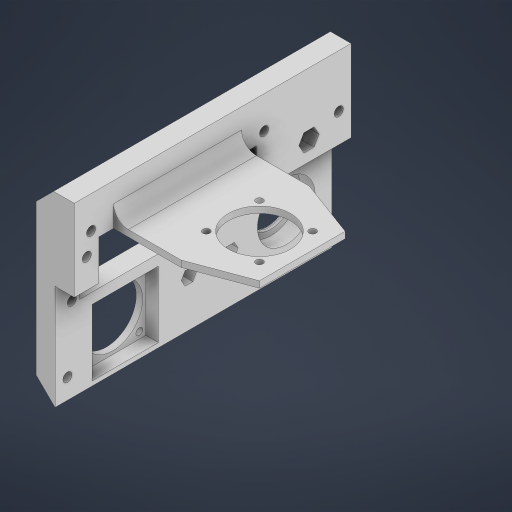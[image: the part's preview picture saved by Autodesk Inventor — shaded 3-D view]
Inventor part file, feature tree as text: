
AUTODESK INVENTOR PART (.ipt)
format: ipt  version: 2024 (Build 280153000, 153)  size: 458,240 bytes
history: native  units: in
note: dims shown in document units (in); Inventor stores cm internally (conversion verified against a paired STEP export)
features: reference x18, extrude x14, sketch x12, other x9, projected_geometry x7, fillet x2, plane x1, chamfer x1
ambient origin geometry x8: Origin, YZ Plane, XZ Plane, XY Plane, X Axis, Y Axis, Z Axis, Center Point
bodies: Solid1 (feature_tree)
feature tree (64):
  sketch  "Sketch1"  dims[d0=0.0787in d1=0.0079in]
  plane  "Work Plane1"
  extrude  "Extrusion1"  Depth=0.0079in
  extrude  "Extrusion2"  Depth=1.0in TaperAngle=0.0deg
  extrude  "Extrusion4"  Depth=0.2362in TaperAngle=0.0deg
  extrude  "Extrusion5"  Depth=0.0669in TaperAngle=0.0deg
  fillet  "Fillet1"  Radius=0.0236in
  extrude  "Extrusion7"  Depth=0.2953in
  extrude  "Extrusion9"  Depth=0.2953in
  extrude  "Extrusion10"  Depth=0.1575in TaperAngle=0.0deg
  extrude  "Extrusion11"  Depth=0.26in
  sketch  "Sketch12"  dims[d35=0.845in d36=0.0in d37=0.3228in]
  extrude  "Extrusion12"  Depth=0.3228in
  extrude  "Extrusion13"  Depth=0.2953in
  extrude  "Extrusion14"  Depth=1.1811in
  extrude  "Extrusion15"  Depth=0.0394in
  extrude  "Extrusion16"  Depth=0.0394in
  extrude  "Extrusion17"  Depth=0.0394in
  fillet  "Fillet2"  Radius=0.0787in
  chamfer  "Chamfer1"  Distance=1.1024in
  reference  "Reference1"
  reference  "Reference2"
  reference  "Reference3"
  reference  "Reference4"
  sketch  "Sketch2"  dims[d2=1.0in d3=0.0in d4=1.0in d5=0.0in]
  reference  "Reference5"
  reference  "Reference6"
  reference  "Reference7"
  reference  "Reference8"
  sketch  "Sketch4"  dims[d10=1.063in d11=0.2362in d12=0.0in]
  projected_geometry  "Projected Loop1"
  sketch  "Sketch5"  dims[d13=0.813in d14=0.0669in d15=0.0in d16=0.0236in]
  sketch  "Sketch7"  dims[d19=0.2953in d20=0.2953in]
  projected_geometry  "Projected Loop3"
  reference  "Reference22"
  reference  "Reference23"
  reference  "Reference24"
  sketch  "Sketch9"  dims[d21=0.2953in d22=0.2953in]
  sketch  "Sketch10"  dims[d23=0.7544in d24=0.0in d31=0.1575in d32=0.0in]
  reference  "Reference28"
  reference  "Reference29"
  reference  "Reference30"
  reference  "Reference31"
  reference  "Reference32"
  sketch  "Sketch11"  dims[d33=0.26in d34=0.26in]
  projected_geometry  "Projected Loop5"
  reference  "Reference33"
  projected_geometry  "Projected Loop6"
  projected_geometry  "Projected Loop7"
  sketch  "Sketch13"  dims[d38=0.845in d39=0.0in d40=0.2953in]
  sketch  "Sketch14"  dims[d41=0.2953in d42=1.1811in]
  projected_geometry  "Projected Loop8"
  sketch  "Sketch15"  dims[d43=1.1811in d44=0.126in d45=0.1004in d46=0.1004in d47=0.0787in d48=1.1024in d49=0.0197in d50=0.5325in d51=0.0in d52=0.5325in d53=0.0in d54=0.1181in d55=0.0in d56=0.2441in d57=0.2441in d58=0.3in d59=0.3in d60=0.4931in d61=0.0in d62=0.1181in d65=2.4931in d66=0.0in d67=1.1811in d68=1.1811in d69=2.3622in d70=0.126in d71=0.1004in d72=0.1004in d73=1.1417in d74=2.4931in d75=0.0in d76=0.2736in d77=0.0394in d78=0.125in d79=45.0deg]
  projected_geometry  "Projected Loop9"
  reference  "Reference34"
  other  "<userpath>\Desktop\SeniorDesign\Head_V3\Head_V3_Assembly.iam"
  other  "Head_V3_Assembly.iam"
  other  "Head_Left_Panel:1"
  other  "Head_base_mount:1"
  other  "Head_Right_Panel:1"
  other  "RaspberryPi_Encloser:1"
  other  "RaspberryPi_IO_Shield:1"
  other  "RaspberryPi_baseplate:1"
  other  "RaspberryPi4:1"
